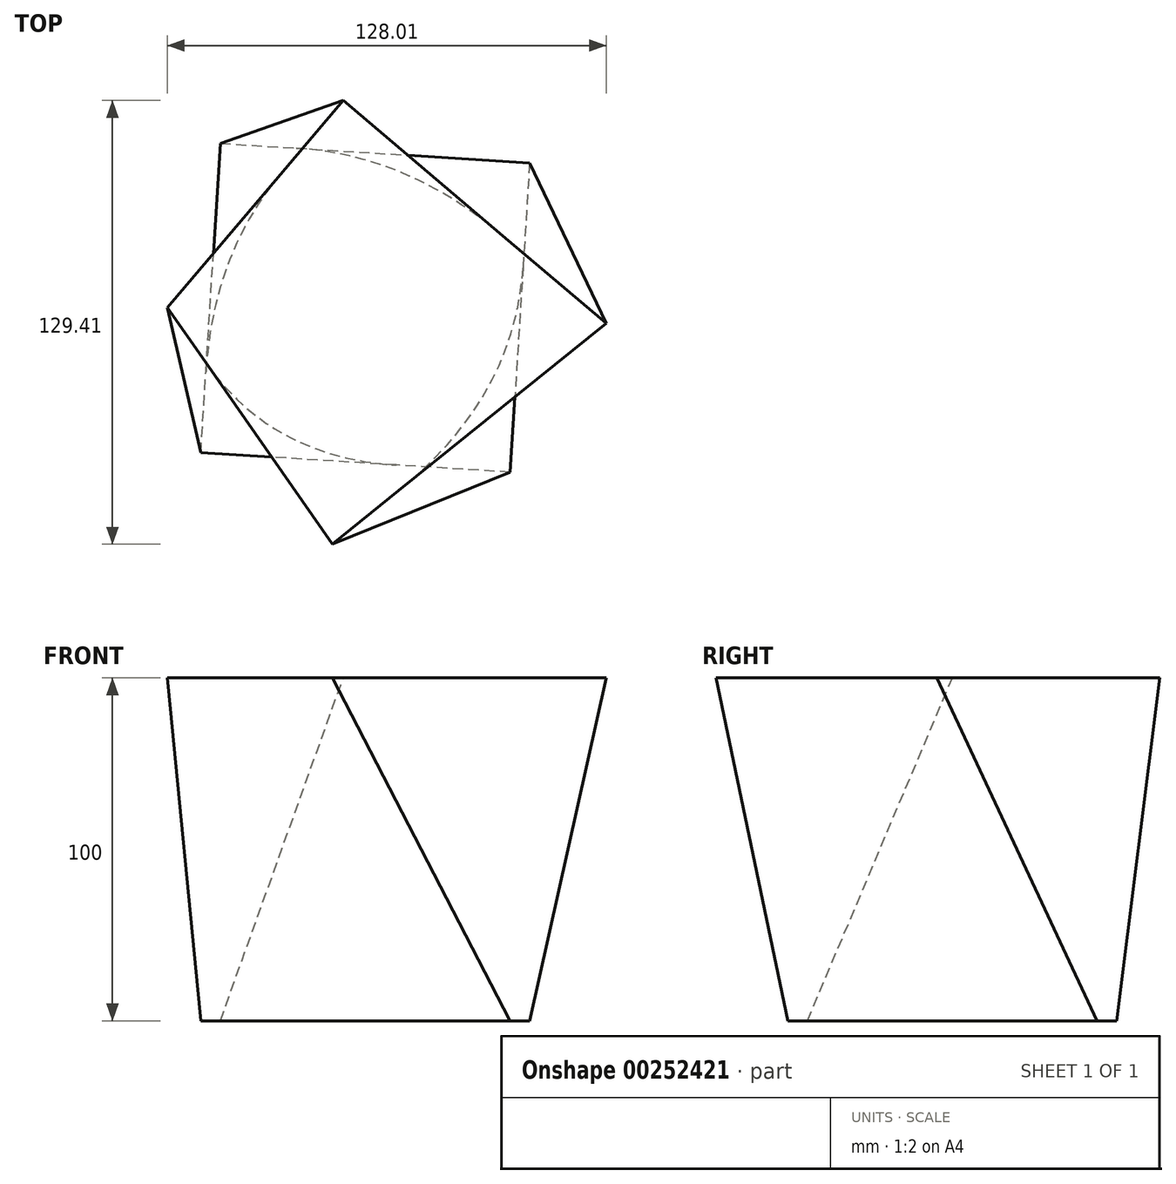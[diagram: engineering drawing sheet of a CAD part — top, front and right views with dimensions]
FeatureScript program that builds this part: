
annotation { "Feature Type Name" : "Feature", "Feature Type Description" : "" }
export const myFeature = defineFeature(function(context is Context, id is Id, definition is map)
    precondition{}
    {
        {
            var Q0;
            Q0=qCreatedBy(makeId("Top.planeOp"),FACE);
            var sketch = newSketch(context, id + "F0", { "sketchPlane" : qUnion([Q0])});
            skCircle(sketch, "E0.cCircle", {"center": v(0, 0) * mm, "radius": 63.92 * mm, "construction": true});
            skLineSegment(sketch, "E0.0", {"start": v(-42.26, 47.95) * mm, "end": v(47.95, 42.26) * mm});
            skLineSegment(sketch, "E0.1", {"start": v(47.95, 42.26) * mm, "end": v(42.26, -47.95) * mm});
            skLineSegment(sketch, "E0.2", {"start": v(42.26, -47.95) * mm, "end": v(-47.95, -42.26) * mm});
            skLineSegment(sketch, "E0.3", {"start": v(-47.95, -42.26) * mm, "end": v(-42.26, 47.95) * mm});
            skSolve(sketch);
        }
        {
            var Q0;
            Q0=qCreatedBy(makeId("Top.planeOp"),FACE);
            cPlane(context, id + "F1", {"entities" : qUnion([Q0]), "cplaneType" : CPlaneType.OFFSET, "offset" : 100 * mm, "width" : 152.4 * mm, "height" : 152.4 * mm});
        }
        {
            var Q0;
            Q0=qCreatedBy(id+"F1.planeOp",FACE);
            var sketch = newSketch(context, id + "F2", { "sketchPlane" : qUnion([Q0])});
            skLineSegment(sketch, "E1", {"start": v(-57.71, 0) * mm, "end": v(-6.41, 60.48) * mm});
            skLineSegment(sketch, "E2", {"start": v(-6.41, 60.48) * mm, "end": v(70.3, -4.59) * mm});
            skLineSegment(sketch, "E3", {"start": v(70.3, -4.59) * mm, "end": v(-9.62, -68.93) * mm});
            skLineSegment(sketch, "E4", {"start": v(-9.62, -68.93) * mm, "end": v(-57.71, 0) * mm});
            skSolve(sketch);
        }
        {
            var Q0;
            Q0=makeQuery(id+"F0.imprint","IMPRINT",FACE,{"disambiguationData":[TD([[makeQuery(id+"F0.imprint","IMPRINT",EDGE,{"derivedFrom":sQuery(id+"F0.wireOp",EDGE,"E0.0")}),-1.0]])]});
            var Q1;
            Q1=makeQuery(id+"F2.imprint","IMPRINT",FACE,{"disambiguationData":[TD([[makeQuery(id+"F2.imprint","IMPRINT",EDGE,{"derivedFrom":sQuery(id+"F2.wireOp",EDGE,"E1")}),-1.0]])]});
            loft(context, id + "F3", {"sheetProfilesArray" : [{ "sheetProfileEntities" : qUnion([Q0]) }, { "sheetProfileEntities" : qUnion([Q1]) }]});
        }
    });
